# Revit family: Hager-IC-Surface_mounted-IP30-Without_Cover-With_DIN-Hosted-PL-pl
name_source: partatom
category: Electrical Equipment
units: mm (PartAtom-declared; Revit-internal decimal feet)

## family parameters
Cut with Voids When Loaded = No
Host = Face
Maintain Annotation Orientation = Yes
Panel Configuration = Two Columns, Circuits Across
Part Type = Panelboard
Room Calculation Point = No
Round Connector Dimension = Use Diameter
Shared = No

## types (10) — shared parameters
BC_MODEL_ID = 1554363
BC_OBJECT_ID = 513889
BC_OBJECT_VERSION = #5
Code hager = ADD-EC000214_EU
EF000003 - Sposób montażu = Montaż natynkowy
EF000007 - Kolor = Biały
EF000024 - Odporność na promieniowanie UV = No
EF000116 - Numer RAL = 9010
EF000118 - Z płytą montażową = No
EF001062 - Wykonanie zgodne z Dyrektywą Kompatybilności Elektromagnetycznej EMC = No
EF001088 - Możliwość rozbudowy = Yes
EF001134 - Szyna DIN = Yes
EF004462 - Rodzaj zamknięcia = Inne
EF005474 - Stopień ochrony (IP) = IP30
EF006244 - Transparentna pokrywa/drzwi = No
EF006306 - Z zamkiem = No
EF009212 - Wykonanie/rodzaj pokrywy = Zamknięty
EF015941 - Drzwi przepuszczające sygnał = Yes
ETIM class code = EC000214
ETIM class name = Small distribution board
HG000001-Number of columns-pl = 1
HG000002-with door or cover-pl = No
HG000003-Range-pl = IC
HG000005-Thickness-pl = 2 mm  [stored 0.00656168 ft]
HG000006-Flush mounted-pl = No
HG000009-Double swing door-pl = No
HG000010-Asymmetric doors-pl = No
HG000011-Empty rows from bottom-pl = No
HG000012-Door swing angle-pl = 90.00°
HG000013-Door on the left-pl = No
HG000014-Door on the right-pl = Yes
HG000015-Clearance visibility-pl = Yes
HG000016-Door 3D visibility-pl = Yes
HG000017-Distance between poles-pl = 18 mm  [stored 0.0590551 ft]
HG000060-RAL-number = 9010
HG000099-Onfly Template ID-pl-PL = 507532
Manufacturer = Hager
Name = IC-Surface_mounted-IP30-Without_Cover-With_DIN-PL
Name BIM&CO = Electricity
Name hager = ADD_Enclosures_EC000214
Uniformat = Low Tension Service & Dist.
Uniformat code = D501001
zero-valued in all types: Default Elevation, EF000218 - Głębokość wbudowania, EF000332 - Wysokość wbudowania, EF000846 - Szerokość wbudowania, EF001131 - Głębokość wewnętrzna, HG000007-Number of empty columns-pl, HG000008-Number of empty rows-pl

## per-type parameters (varying)
| type | BC_VARIANT_ID | EF000008 - Szerokość | EF000040 - Wysokość | EF000049 - Głębokość | EF000266 - Liczba rzędów | EF002950 - Szerokość wyrażona liczbą modułów | EF015776 - Listwa zaciskowa uziemienia | EF015777 - Listwa zaciskowa przewodu neutralnego | HG000004-Manufacturer reference-pl | HGEF000266-Liczba rzędów | HGEF0002950-Szerokość wyrażona liczbą modułów |
| IC-Surface_mounted_W27_H163_D71_1_Modular_Spacing-VD101NE | 1179024 | 27 mm  [stored 0.0885827 ft] | 163 mm  [stored 0.534777 ft] | 71 mm  [stored 0.23294 ft] | 1 | 1 | No | No | VD101NE | 1 | 1 |
| IC-Surface_mounted_W45_H163_D71_2_Modular_Spacing-VD102NE | 1179025 | 45 mm  [stored 0.147638 ft] | 163 mm  [stored 0.534777 ft] | 71 mm  [stored 0.23294 ft] | 1 | 2 | No | No | VD102NE | 1 | 2 |
| IC-Surface_mounted_W63_H163_D71_3_Modular_Spacing-VD103NE | 1179026 | 63 mm  [stored 0.206693 ft] | 163 mm  [stored 0.534777 ft] | 71 mm  [stored 0.23294 ft] | 1 | 3 | No | No | VD103NE | 1 | 3 |
| IC-Surface_mounted_W81_H163_D71_4_Modular_Spacing-VD104NE | 1179027 | 81 mm  [stored 0.265748 ft] | 163 mm  [stored 0.534777 ft] | 71 mm  [stored 0.23294 ft] | 1 | 4 | No | No | VD104NE | 1 | 4 |
| IC-Surface_mounted_W134_H170_D91_6_Modular_Spacing-VD106NP | 1179028 | 134 mm | 170 mm  [stored 0.557743 ft] | 91 mm  [stored 0.298556 ft] | 1 | 6 | Yes | Yes | VD106NP | 1 | 6 |
| IC-Surface_mounted_W170_H170_D91_8_Modular_Spacing-VD108NP | 1179029 | 170 mm  [stored 0.557743 ft] | 170 mm  [stored 0.557743 ft] | 91 mm  [stored 0.298556 ft] | 1 | 8 | Yes | Yes | VD108NP | 1 | 8 |
| IC-Surface_mounted_W206_H170_D91_10_Modular_Spacing-VD110NP | 1179030 | 206 mm  [stored 0.675853 ft] | 170 mm  [stored 0.557743 ft] | 91 mm  [stored 0.298556 ft] | 1 | 10 | Yes | Yes | VD110NP | 1 | 10 |
| IC-Surface_mounted_W292_H200_D91_12_Modular_Spacing-VD112NP | 1179031 | 292 mm  [stored 0.958005 ft] | 200 mm  [stored 0.656168 ft] | 91 mm  [stored 0.298556 ft] | 1 | 12 | Yes | Yes | VD112NP | 1 | 12 |
| IC-Surface_mounted_W400_H200_D91_18_Modular_Spacing-VD118NP | 1179032 | 400 mm  [stored 1.31234 ft] | 200 mm  [stored 0.656168 ft] | 91 mm  [stored 0.298556 ft] | 1 | 18 | Yes | Yes | VD118NP | 1 | 18 |
| IC-Surface_mounted_W294_H326_D92_12_Modular_Spacing-VD212NP | 1179033 | 294 mm  [stored 0.964567 ft] | 326 mm  [stored 1.06955 ft] | 92 mm  [stored 0.301837 ft] | 2 | 12 | Yes | Yes | VD212NP | 2 | 12 |

note: column(s) folded — value = type name in every type: Reference

note: [stored X ft] marks values corroborated as IEEE doubles in the binary element streams (Revit-internal decimal feet)

## geometry (parser evidence)
native form markers: Sweep x14
no freeform markers — native parametric forms only
